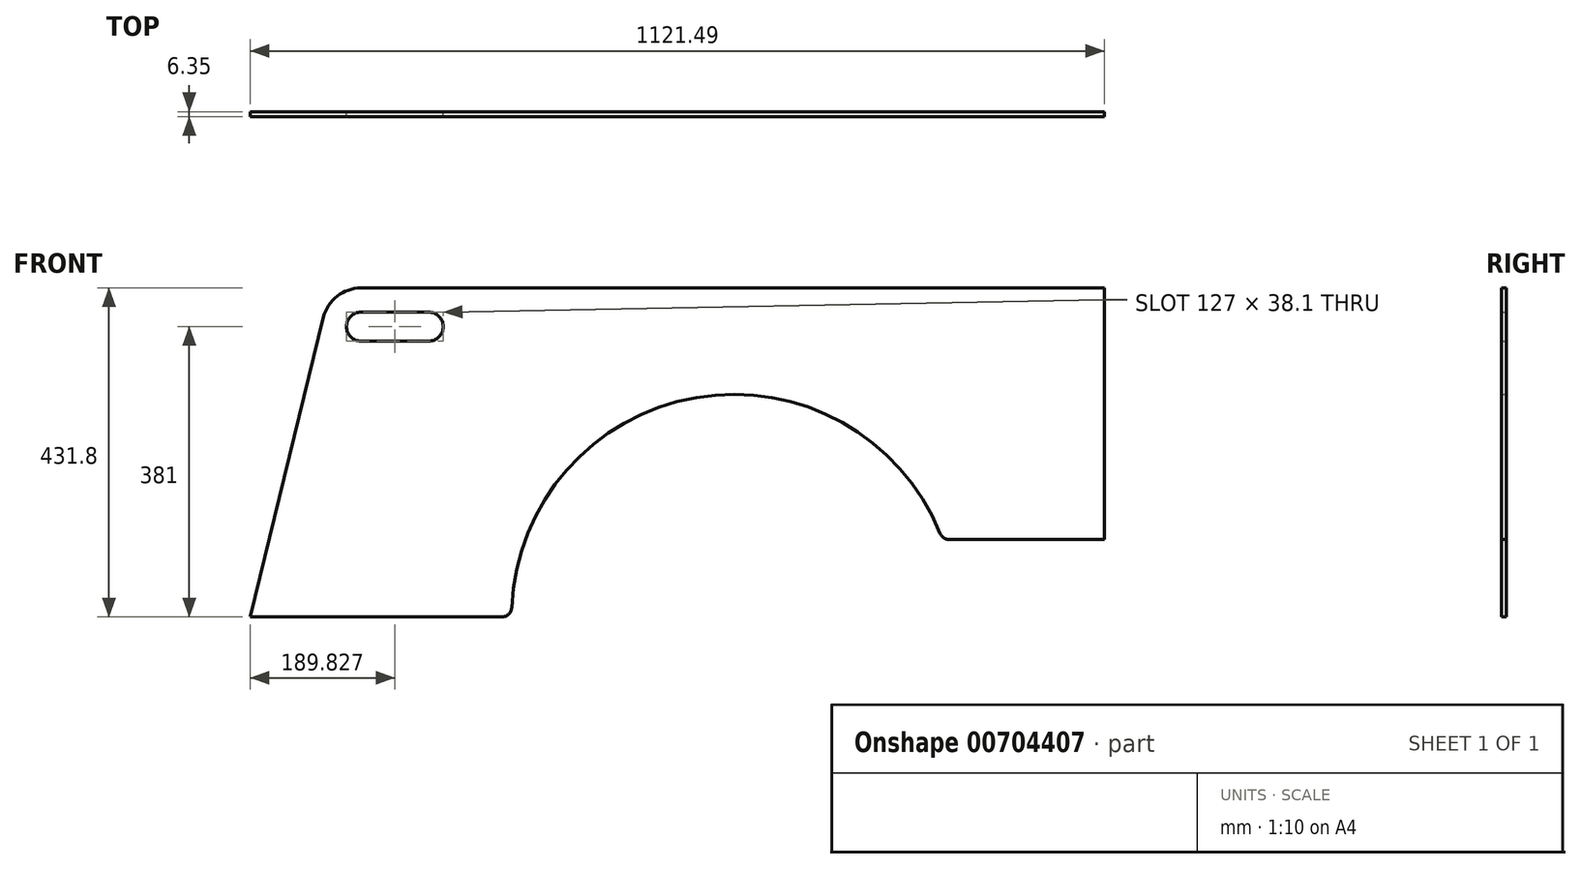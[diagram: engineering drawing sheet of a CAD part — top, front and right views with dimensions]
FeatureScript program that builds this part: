
annotation { "Feature Type Name" : "Feature", "Feature Type Description" : "" }
export const myFeature = defineFeature(function(context is Context, id is Id, definition is map)
    precondition{}
    {
        {
            var Q0;
            Q0=qCreatedBy(makeId("Front.planeOp"),FACE);
            var sketch = newSketch(context, id + "F0", { "sketchPlane" : qUnion([Q0])});
            skLineSegment(sketch, "E0", {"start": v(0, 0) * mm, "end": v(96.03, 393.06) * mm});
            skLineSegment(sketch, "E1", {"start": v(145.38, 431.8) * mm, "end": v(1121.5, 431.8) * mm});
            skLineSegment(sketch, "E2", {"start": v(1121.5, 431.8) * mm, "end": v(1121.5, 0) * mm});
            skLineSegment(sketch, "E3.trimOffspring", {"start": v(330.46, 0) * mm, "end": v(0, 0) * mm});
            skArc(sketch, "E4", {"start": v(905.78, 109.54) * mm, "mid": v(585.2, 287.82) * mm, "end": v(343.15, 12.17) * mm});
            skLineSegment(sketch, "E5", {"start": v(342.9, 0) * mm, "end": v(927.1, 0) * mm, "construction": true});
            skLineSegment(sketch, "E6", {"start": v(927.1, 0) * mm, "end": v(1121.5, 0) * mm});
            skLineSegment(sketch, "E7", {"start": v(1121.5, 101.6) * mm, "end": v(917.56, 101.6) * mm});
            skPoint(sketch, "E8.visualSharp", {"position": v(342.9, 0) * mm});
            skArc(sketch, "E8.filletArc", {"start": v(330.46, 0) * mm, "mid": v(339.26, 3.53) * mm, "end": v(343.15, 12.17) * mm});
            skPoint(sketch, "E9.visualSharp", {"position": v(927.1, 0) * mm});
            skPoint(sketch, "E10.visualSharp", {"position": v(105.5, 431.8) * mm});
            skArc(sketch, "E10.filletArc", {"start": v(145.38, 431.8) * mm, "mid": v(114, 420.96) * mm, "end": v(96.03, 393.06) * mm});
            skArc(sketch, "E11", {"start": v(145.38, 400.05) * mm, "mid": v(126.33, 381) * mm, "end": v(145.38, 361.95) * mm});
            skLineSegment(sketch, "E12", {"start": v(145.38, 381) * mm, "end": v(234.28, 381) * mm, "construction": true});
            skArc(sketch, "E13", {"start": v(234.28, 361.95) * mm, "mid": v(253.33, 381) * mm, "end": v(234.28, 400.05) * mm});
            skLineSegment(sketch, "E14", {"start": v(234.28, 400.05) * mm, "end": v(145.38, 400.05) * mm});
            skLineSegment(sketch, "E15", {"start": v(145.38, 361.95) * mm, "end": v(234.28, 361.95) * mm});
            skPoint(sketch, "E16.visualSharp", {"position": v(908.86, 101.6) * mm});
            skArc(sketch, "E16.filletArc", {"start": v(905.78, 109.54) * mm, "mid": v(910.46, 103.77) * mm, "end": v(917.56, 101.6) * mm});
            skSolve(sketch);
        }
        {
            var Q0;
            Q0=makeQuery(id+"F0.imprint","IMPRINT",FACE,{"disambiguationData":[TD([[makeQuery(id+"F0.imprint","IMPRINT",EDGE,{"derivedFrom":sQuery(id+"F0.wireOp",EDGE,"E0")}),-1.0]])]});
            extrude(context, id + "F1", {"entities" : qUnion([Q0]), "depth" : 6.35 * mm, "offsetDistance" : 25.4 * mm});
        }
    });
